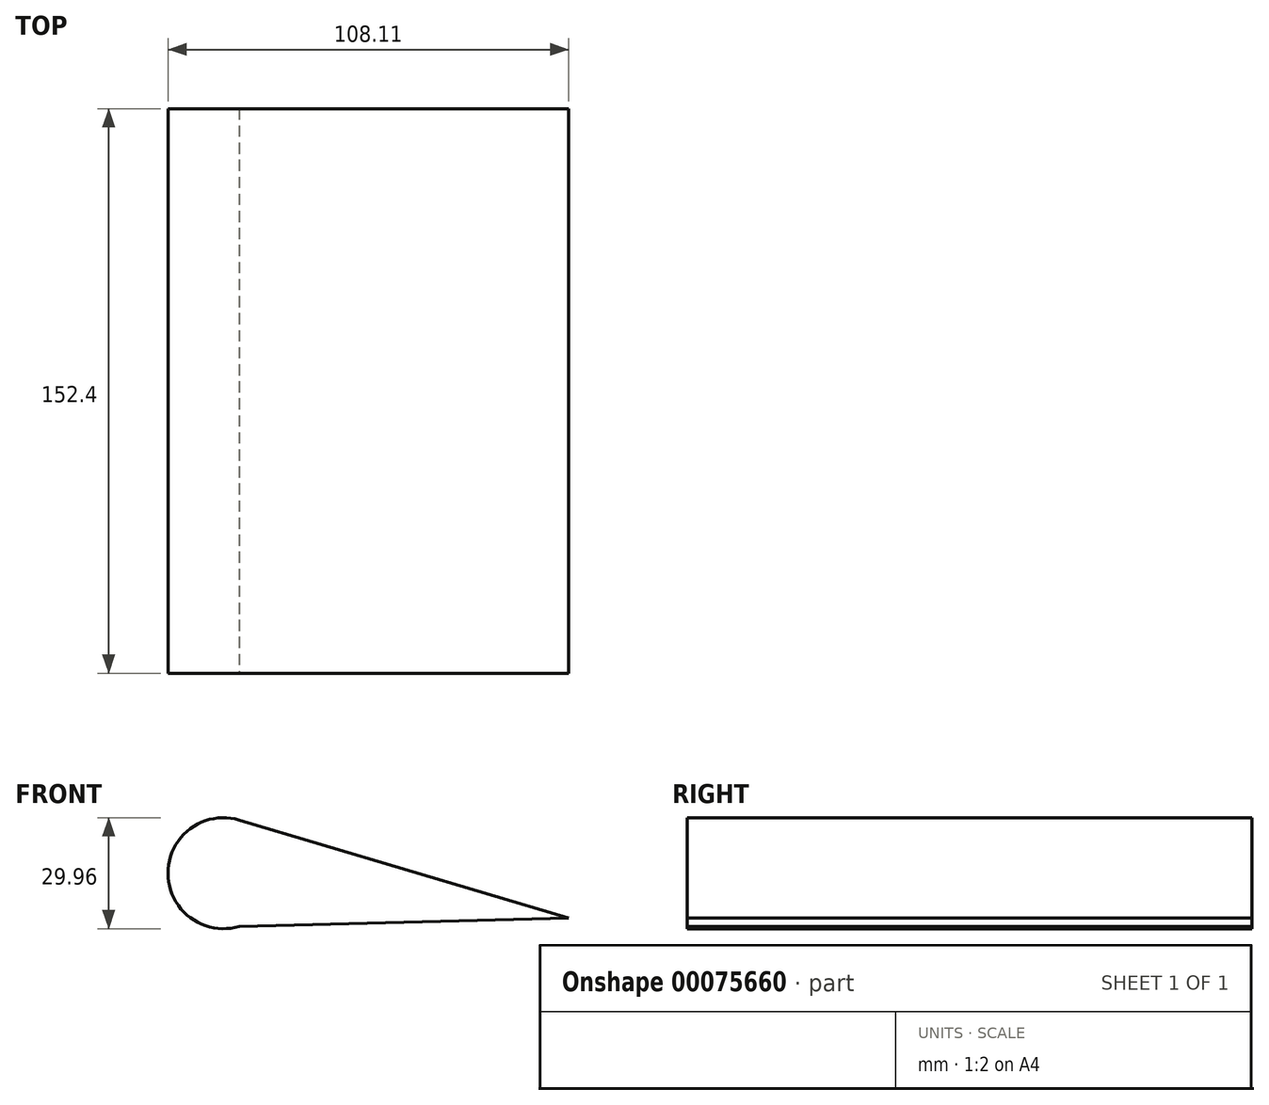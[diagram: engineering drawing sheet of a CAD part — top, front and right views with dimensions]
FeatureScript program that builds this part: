
annotation { "Feature Type Name" : "Feature", "Feature Type Description" : "" }
export const myFeature = defineFeature(function(context is Context, id is Id, definition is map)
    precondition{}
    {
        {
            var Q0;
            Q0=qCreatedBy(makeId("Front.planeOp"),FACE);
            var sketch = newSketch(context, id + "F0", { "sketchPlane" : qUnion([Q0])});
            skLineSegment(sketch, "E0", {"start": v(2.1, 44.42) * mm, "end": v(90.97, 17.99) * mm});
            skLineSegment(sketch, "E1", {"start": v(90.97, 17.99) * mm, "end": v(2.1, 15.7) * mm});
            skArc(sketch, "E2", {"start": v(2.1, 44.42) * mm, "mid": v(-17.14, 30.06) * mm, "end": v(2.1, 15.7) * mm});
            skSolve(sketch);
        }
        {
            var Q0;
            Q0=qCreatedBy(makeId("Front.planeOp"),FACE);
            cPlane(context, id + "F1", {"entities" : qUnion([Q0]), "cplaneType" : CPlaneType.OFFSET, "offset" : 152.4 * mm, "width" : 152.4 * mm, "height" : 152.4 * mm});
        }
        {
            var Q0;
            Q0=qCreatedBy(id+"F1.planeOp",FACE);
            var sketch = newSketch(context, id + "F2", { "sketchPlane" : qUnion([Q0])});
            skLineSegment(sketch, "E3.0", {"start": v(90.97, 17.99) * mm, "end": v(2.1, 15.7) * mm});
            skArc(sketch, "E4.0", {"start": v(2.1, 44.42) * mm, "mid": v(-17.14, 30.06) * mm, "end": v(2.1, 15.7) * mm});
            skLineSegment(sketch, "E5.0", {"start": v(2.1, 44.42) * mm, "end": v(90.97, 17.99) * mm});
            skSolve(sketch);
        }
        {
            var Q0;
            Q0=makeQuery(id+"F0.imprint","IMPRINT",FACE,{"disambiguationData":[TD([[makeQuery(id+"F0.imprint","IMPRINT",EDGE,{"derivedFrom":sQuery(id+"F0.wireOp",EDGE,"E0")}),-1.0]])]});
            var Q1;
            Q1=makeQuery(id+"F2.imprint","IMPRINT",FACE,{"disambiguationData":[TD([[makeQuery(id+"F2.imprint","IMPRINT",EDGE,{"derivedFrom":sQuery(id+"F2.wireOp",EDGE,"E3.0")}),-1.0]])]});
            loft(context, id + "F3", {"sheetProfilesArray" : [{ "sheetProfileEntities" : qUnion([Q0]) }, { "sheetProfileEntities" : qUnion([Q1]) }]});
        }
    });
